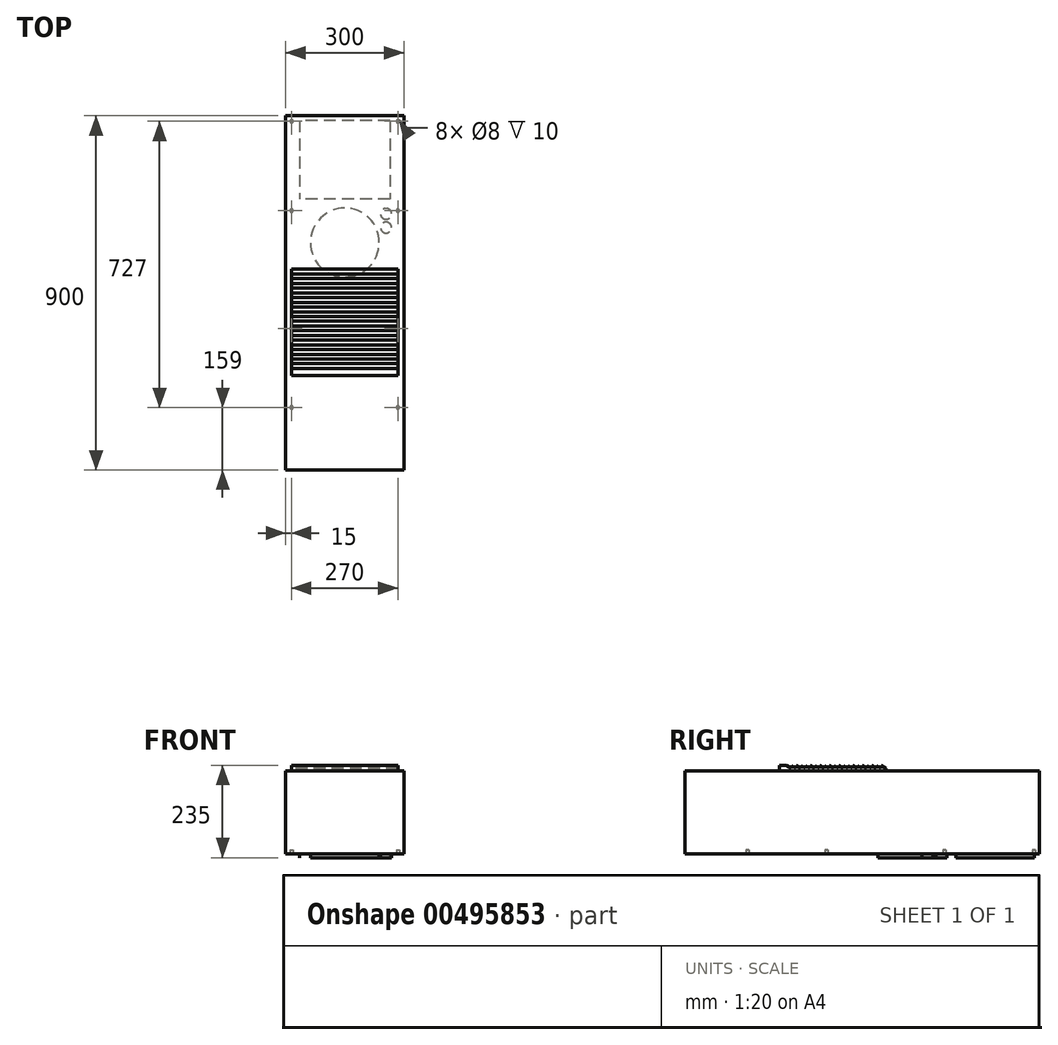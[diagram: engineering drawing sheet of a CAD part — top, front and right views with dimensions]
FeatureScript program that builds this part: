
annotation { "Feature Type Name" : "Feature", "Feature Type Description" : "" }
export const myFeature = defineFeature(function(context is Context, id is Id, definition is map)
    precondition{}
    {
        {
            var Q0;
            Q0=qCreatedBy(makeId("Top.planeOp"),FACE);
            var sketch = newSketch(context, id + "F0", { "sketchPlane" : qUnion([Q0])});
            skLineSegment(sketch, "E0.bottom", {"start": v(150, 450) * mm, "end": v(-150, 450) * mm});
            skLineSegment(sketch, "E0.top", {"start": v(150, -450) * mm, "end": v(-150, -450) * mm});
            skLineSegment(sketch, "E0.left", {"start": v(150, 450) * mm, "end": v(150, -450) * mm});
            skLineSegment(sketch, "E0.right", {"start": v(-150, 450) * mm, "end": v(-150, -450) * mm});
            skPoint(sketch, "E0.middle", {"position": v(0, 0) * mm});
            skSolve(sketch);
        }
        {
            var Q0;
            Q0=qSketchRegion(id+"F0",true);
            extrude(context, id + "F1", {"entities" : qUnion([Q0]), "depth" : 210 * mm});
        }
        {
            var Q0;
            Q0=makeQuery(id+"F1.opExtrude","CAP_FACE",FACE,{"disambiguationData":[OSD([sQuery(id+"F0.wireOp",EDGE,"E0.bottom"),sQuery(id+"F0.wireOp",EDGE,"E0.top"),sQuery(id+"F0.wireOp",EDGE,"E0.left"),sQuery(id+"F0.wireOp",EDGE,"E0.right")])],"isStart":false});
            var sketch = newSketch(context, id + "F2", { "sketchPlane" : qUnion([Q0])});
            skLineSegment(sketch, "E1.bottom", {"start": v(-135, 60) * mm, "end": v(135, 60) * mm});
            skLineSegment(sketch, "E1.top", {"start": v(-135, -210) * mm, "end": v(135, -210) * mm});
            skLineSegment(sketch, "E1.left", {"start": v(-135, 60) * mm, "end": v(-135, -210) * mm});
            skLineSegment(sketch, "E1.right", {"start": v(135, 60) * mm, "end": v(135, -210) * mm});
            skSolve(sketch);
        }
        {
            var Q0;
            Q0=qSketchRegion(id+"F2",true);
            extrude(context, id + "F3", {"entities" : qUnion([Q0]), "depth" : 15 * mm});
        }
        {
            var Q0;
            Q0=makeQuery(id+"F3.opExtrude","SWEPT_FACE",FACE,{"disambiguationData":[OSD([sQuery(id+"F2.wireOp",EDGE,"E1.left")])]});
            var sketch = newSketch(context, id + "F4", { "sketchPlane" : qUnion([Q0])});
            skLineSegment(sketch, "E2", {"start": v(-60, 217.5) * mm, "end": v(-48, 225) * mm});
            skLineSegment(sketch, "E3", {"start": v(-48, 225) * mm, "end": v(-48, 217.5) * mm});
            skLineSegment(sketch, "E4.1.0.0", {"start": v(-48, 217.5) * mm, "end": v(-36, 225) * mm});
            skLineSegment(sketch, "E4.1.0.1", {"start": v(-36, 225) * mm, "end": v(-36, 217.5) * mm});
            skLineSegment(sketch, "E4.2.0.0", {"start": v(-36, 217.5) * mm, "end": v(-24, 225) * mm});
            skLineSegment(sketch, "E4.2.0.1", {"start": v(-24, 225) * mm, "end": v(-24, 217.5) * mm});
            skLineSegment(sketch, "E4.3.0.0", {"start": v(-24, 217.5) * mm, "end": v(-12, 225) * mm});
            skLineSegment(sketch, "E4.3.0.1", {"start": v(-12, 225) * mm, "end": v(-12, 217.5) * mm});
            skLineSegment(sketch, "E4.4.0.0", {"start": v(-12, 217.5) * mm, "end": v(0, 225) * mm});
            skLineSegment(sketch, "E4.4.0.1", {"start": v(0, 225) * mm, "end": v(0, 217.5) * mm});
            skLineSegment(sketch, "E4.5.0.0", {"start": v(0, 217.5) * mm, "end": v(12, 225) * mm});
            skLineSegment(sketch, "E4.5.0.1", {"start": v(12, 225) * mm, "end": v(12, 217.5) * mm});
            skLineSegment(sketch, "E4.6.0.0", {"start": v(12, 217.5) * mm, "end": v(24, 225) * mm});
            skLineSegment(sketch, "E4.6.0.1", {"start": v(24, 225) * mm, "end": v(24, 217.5) * mm});
            skLineSegment(sketch, "E4.7.0.0", {"start": v(24, 217.5) * mm, "end": v(36, 225) * mm});
            skLineSegment(sketch, "E4.7.0.1", {"start": v(36, 225) * mm, "end": v(36, 217.5) * mm});
            skLineSegment(sketch, "E4.8.0.0", {"start": v(36, 217.5) * mm, "end": v(48, 225) * mm});
            skLineSegment(sketch, "E4.8.0.1", {"start": v(48, 225) * mm, "end": v(48, 217.5) * mm});
            skLineSegment(sketch, "E4.9.0.0", {"start": v(48, 217.5) * mm, "end": v(60, 225) * mm});
            skLineSegment(sketch, "E4.9.0.1", {"start": v(60, 225) * mm, "end": v(60, 217.5) * mm});
            skLineSegment(sketch, "E4.10.0.0", {"start": v(60, 217.5) * mm, "end": v(72, 225) * mm});
            skLineSegment(sketch, "E4.10.0.1", {"start": v(72, 225) * mm, "end": v(72, 217.5) * mm});
            skLineSegment(sketch, "E4.11.0.0", {"start": v(72, 217.5) * mm, "end": v(84, 225) * mm});
            skLineSegment(sketch, "E4.11.0.1", {"start": v(84, 225) * mm, "end": v(84, 217.5) * mm});
            skLineSegment(sketch, "E4.12.0.0", {"start": v(84, 217.5) * mm, "end": v(96, 225) * mm});
            skLineSegment(sketch, "E4.12.0.1", {"start": v(96, 225) * mm, "end": v(96, 217.5) * mm});
            skLineSegment(sketch, "E4.13.0.0", {"start": v(96, 217.5) * mm, "end": v(108, 225) * mm});
            skLineSegment(sketch, "E4.13.0.1", {"start": v(108, 225) * mm, "end": v(108, 217.5) * mm});
            skLineSegment(sketch, "E4.14.0.0", {"start": v(108, 217.5) * mm, "end": v(120, 225) * mm});
            skLineSegment(sketch, "E4.14.0.1", {"start": v(120, 225) * mm, "end": v(120, 217.5) * mm});
            skLineSegment(sketch, "E4.15.0.0", {"start": v(120, 217.5) * mm, "end": v(132, 225) * mm});
            skLineSegment(sketch, "E4.15.0.1", {"start": v(132, 225) * mm, "end": v(132, 217.5) * mm});
            skLineSegment(sketch, "E4.16.0.0", {"start": v(132, 217.5) * mm, "end": v(144, 225) * mm});
            skLineSegment(sketch, "E4.16.0.1", {"start": v(144, 225) * mm, "end": v(144, 217.5) * mm});
            skLineSegment(sketch, "E4.17.0.0", {"start": v(144, 217.5) * mm, "end": v(156, 225) * mm});
            skLineSegment(sketch, "E4.17.0.1", {"start": v(156, 225) * mm, "end": v(156, 217.5) * mm});
            skLineSegment(sketch, "E4.18.0.0", {"start": v(156, 217.5) * mm, "end": v(168, 225) * mm});
            skLineSegment(sketch, "E4.18.0.1", {"start": v(168, 225) * mm, "end": v(168, 217.5) * mm});
            skLineSegment(sketch, "E4.19.0.0", {"start": v(168, 217.5) * mm, "end": v(180, 225) * mm});
            skLineSegment(sketch, "E4.19.0.1", {"start": v(180, 225) * mm, "end": v(180, 217.5) * mm});
            skLineSegment(sketch, "E4.20.0.0", {"start": v(180, 217.5) * mm, "end": v(192, 225) * mm});
            skLineSegment(sketch, "E4.direction1", {"start": v(-60, 217.5) * mm, "end": v(-48, 217.5) * mm, "construction": true});
            skLineSegment(sketch, "E5", {"start": v(-60, 217.5) * mm, "end": v(-68.77, 217.5) * mm});
            skLineSegment(sketch, "E6", {"start": v(-68.77, 217.5) * mm, "end": v(-68.77, 249.12) * mm});
            skLineSegment(sketch, "E7", {"start": v(-68.77, 249.12) * mm, "end": v(192, 249.12) * mm});
            skLineSegment(sketch, "E8", {"start": v(192, 249.12) * mm, "end": v(192, 225) * mm});
            skSolve(sketch);
        }
        {
            var Q0;
            Q0=qSketchRegion(id+"F4",true);
            extrude(context, id + "F5", {"entities" : qUnion([Q0]), "operationType" : NewBodyOperationType.REMOVE, "oppositeDirection" : true, "depth" : 312.33 * mm});
        }
        {
            var Q0;
            Q0=makeQuery(id+"F1.opExtrude","CAP_FACE",FACE,{"disambiguationData":[OSD([sQuery(id+"F0.wireOp",EDGE,"E0.bottom"),sQuery(id+"F0.wireOp",EDGE,"E0.top"),sQuery(id+"F0.wireOp",EDGE,"E0.left"),sQuery(id+"F0.wireOp",EDGE,"E0.right")])],"isStart":true});
            var sketch = newSketch(context, id + "F6", { "sketchPlane" : qUnion([Q0])});
            skLineSegment(sketch, "E9.bottom", {"start": v(115, -438) * mm, "end": v(-115, -438) * mm});
            skLineSegment(sketch, "E9.top", {"start": v(115, -238) * mm, "end": v(-115, -238) * mm});
            skLineSegment(sketch, "E9.left", {"start": v(115, -438) * mm, "end": v(115, -238) * mm});
            skLineSegment(sketch, "E9.right", {"start": v(-115, -438) * mm, "end": v(-115, -238) * mm});
            skCircle(sketch, "E10", {"center": v(135, -436) * mm, "radius": 4 * mm});
            skCircle(sketch, "E11", {"center": v(135, -209) * mm, "radius": 4 * mm});
            skCircle(sketch, "E12", {"center": v(135, 91) * mm, "radius": 4 * mm});
            skCircle(sketch, "E13", {"center": v(135, 291) * mm, "radius": 4 * mm});
            skCircle(sketch, "E14", {"center": v(-135, -436) * mm, "radius": 4 * mm});
            skCircle(sketch, "E15", {"center": v(-135, -209) * mm, "radius": 4 * mm});
            skCircle(sketch, "E16", {"center": v(-135, 91) * mm, "radius": 4 * mm});
            skCircle(sketch, "E17", {"center": v(-135, 291) * mm, "radius": 4 * mm});
            skCircle(sketch, "E18", {"center": v(0, -128) * mm, "radius": 87.5 * mm});
            skCircle(sketch, "E19", {"center": v(105, -201) * mm, "radius": 14 * mm});
            skCircle(sketch, "E20", {"center": v(105, -166) * mm, "radius": 14 * mm});
            skSolve(sketch);
        }
        {
            var Q0;
            Q0=makeQuery(id+"F6.imprint","IMPRINT",FACE,{"disambiguationData":[TD([[makeQuery(id+"F6.imprint","IMPRINT",EDGE,{"derivedFrom":sQuery(id+"F6.wireOp",EDGE,"E9.bottom")}),-1.0]])]});
            var Q1;
            Q1=makeQuery(id+"F6.imprint","IMPRINT",FACE,{"disambiguationData":[TD([[makeQuery(id+"F6.imprint","IMPRINT",EDGE,{"derivedFrom":sQuery(id+"F6.wireOp",EDGE,"E18")}),1.0]])]});
            var Q2;
            Q2=makeQuery(id+"F6.imprint","IMPRINT",FACE,{"disambiguationData":[TD([[makeQuery(id+"F6.imprint","IMPRINT",EDGE,{"derivedFrom":sQuery(id+"F6.wireOp",EDGE,"E19")}),1.0]])]});
            var Q3;
            Q3=makeQuery(id+"F6.imprint","IMPRINT",FACE,{"disambiguationData":[TD([[makeQuery(id+"F6.imprint","IMPRINT",EDGE,{"derivedFrom":sQuery(id+"F6.wireOp",EDGE,"E20")}),1.0]])]});
            extrude(context, id + "F7", {"entities" : qUnion([Q0, Q1, Q2, Q3]), "depth" : 10 * mm});
        }
        {
            var Q0;
            Q0=makeQuery(id+"F6.imprint","IMPRINT",FACE,{"disambiguationData":[TD([[makeQuery(id+"F6.imprint","IMPRINT",EDGE,{"derivedFrom":sQuery(id+"F6.wireOp",EDGE,"E10")}),1.0]])]});
            var Q1;
            Q1=makeQuery(id+"F6.imprint","IMPRINT",FACE,{"disambiguationData":[TD([[makeQuery(id+"F6.imprint","IMPRINT",EDGE,{"derivedFrom":sQuery(id+"F6.wireOp",EDGE,"E11")}),1.0]])]});
            var Q2;
            Q2=makeQuery(id+"F6.imprint","IMPRINT",FACE,{"disambiguationData":[TD([[makeQuery(id+"F6.imprint","IMPRINT",EDGE,{"derivedFrom":sQuery(id+"F6.wireOp",EDGE,"E12")}),1.0]])]});
            var Q3;
            Q3=makeQuery(id+"F6.imprint","IMPRINT",FACE,{"disambiguationData":[TD([[makeQuery(id+"F6.imprint","IMPRINT",EDGE,{"derivedFrom":sQuery(id+"F6.wireOp",EDGE,"E13")}),1.0]])]});
            var Q4;
            Q4=makeQuery(id+"F6.imprint","IMPRINT",FACE,{"disambiguationData":[TD([[makeQuery(id+"F6.imprint","IMPRINT",EDGE,{"derivedFrom":sQuery(id+"F6.wireOp",EDGE,"E17")}),1.0]])]});
            var Q5;
            Q5=makeQuery(id+"F6.imprint","IMPRINT",FACE,{"disambiguationData":[TD([[makeQuery(id+"F6.imprint","IMPRINT",EDGE,{"derivedFrom":sQuery(id+"F6.wireOp",EDGE,"E16")}),1.0]])]});
            var Q6;
            Q6=makeQuery(id+"F6.imprint","IMPRINT",FACE,{"disambiguationData":[TD([[makeQuery(id+"F6.imprint","IMPRINT",EDGE,{"derivedFrom":sQuery(id+"F6.wireOp",EDGE,"E15")}),1.0]])]});
            var Q7;
            Q7=makeQuery(id+"F6.imprint","IMPRINT",FACE,{"disambiguationData":[TD([[makeQuery(id+"F6.imprint","IMPRINT",EDGE,{"derivedFrom":sQuery(id+"F6.wireOp",EDGE,"E14")}),1.0]])]});
            extrude(context, id + "F8", {"entities" : qUnion([Q0, Q1, Q2, Q3, Q4, Q5, Q6, Q7]), "operationType" : NewBodyOperationType.REMOVE, "oppositeDirection" : true, "depth" : 10 * mm});
        }
    });
